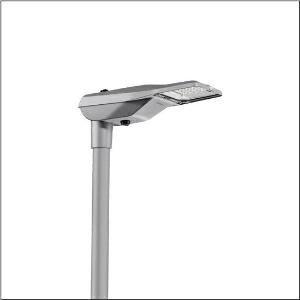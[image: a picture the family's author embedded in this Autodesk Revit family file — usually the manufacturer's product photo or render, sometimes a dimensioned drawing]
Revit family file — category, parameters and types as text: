
# Revit family: streetlight_sl_21_iq_micro___st1_0a_5xe1d51y08cb_5320
name_source: partatom
category: Lighting Fixtures
units: mm (PartAtom-declared; Revit-internal decimal feet)

## family parameters
Cut with Voids When Loaded = No
Host = Face
Light Source = No
Part Type = Normal
Room Calculation Point = No
Round Connector Dimension = Use Diameter
Shared = No

## types (1)
- --- (1 x LED, 2530 lm, 19.1 W, 3000K)
    Apparent Load = 19 VA
    CIE Flux Codes = 37 72 97 100 100
    Color Rendering = 80
    Color Temperature = 3000K
    Default Elevation = 1800 mm
    Description = Streetlight SL 21 iQ micro, mast luminaire, primary light control with lens, of PMMA, primary optical cover: cover, of toughened safety glass, transparent, light distribution: ST1.0a, light emission: direct distribution, primary light characteristic: asymmetric, installation type: post-top, side-entry, LED, High Power LED, rated luminous flux: 2.530lm, luminous efficacy: 133lm/W, light colour: 830, colour temperature: 3000K, control gear: iQ-Street Remote, D4i with power reduction, control: pre-setting: logarithmic dimming characteristic, Street-Remote, Auto-Match, Temp-Guard, Lumen-Switch, Night-Set, Smart-Wire, Light-Fading, Desk-Remote (wireless, voltage-free reading and setting of iQ features in the workshop via application-optimized NFC function/RFID function), optimised constant luminous flux control (CLO 2.0), mains connection: 220..240V, AC, 50/60Hz, start of lifetime: 19W, end of service life: 20W, reduction: 9W, luminaire housing, of diecast aluminium, powder-coated, Siteco® metallic grey (DB 702S), corrosivity category C5 high according to DIN EN ISO 12944, please order mast flange separately, inclination adjustable: 0°, 5°, 10°, 15°, sealing non-destructively replaceable, multi-level sealing system, length: 528mm, width: 235mm, height: 110mm, mast flange for spigot size: 42mm (side-entry): 5XC10008XM4, 60/48mm (side-entry/post-top): 5XC10108XM2, 76/60mm (side-entry/post-top): 5XC10108XM1, mounting height: 4..8m, Smart Interface below and above, protection rating (complete): IP66, insulation class (complete): insulation class II (safety insulation), certification: CE, ENEC, ENEC+, VDE, impact resistance: IK10, permissible operating ambient temperature for outdoor applications: -40..+50°C, standard-compliant lighting for roads and squares, packaging unit: 1 piece

Light Distribution: ST1.0a
    Height = 110 mm
    Lamp = 1 x LED
    Lamp Light Flux = 2530 lm
    Lamp Power = 19.1 W
    Lamp count = 1
    Length = 528 mm
    Luminous efficacy = 132 lm/W
    Manufacturer = Siteco
    ModVariant = No
    Model = 5XE1D51Y08CB
    Number of Poles = 1
    OnlyDefault = Yes
    Power Factor = 1
    Product Name = Streetlight SL 21 iQ micro | ST1.0a
    Product group = mast luminaire | pylon top
    ProductGroupID = 6100
    Protection Class = Protection class II
    Protection Degree = IP 66
    RLX_Detail_Level = 1
    RLX_Emergency_Light_Flux = 0 lm
    RLX_Emergency_Type = 0
    RLX_Emergency_Type_DB = No
    RlxData = <blob elided: 98473 chars, md5=553108e6>
    Socket = socket
    Standby Power = 0 W
    System Light Flux = 2530 lm
    System Power = 19 W
    Type Comments = factory setting: luminous flux: 100 % | dim-lin: 254 | 387 mA
    Type Image = l_1007239.jpg
    URL = http://relux.com
    VarID = @adj_119285
    Voltage = 0 V
    Weight = 0.00 kg
    Width = 235 mm

## geometry (parser evidence)
native form markers: Blend x4, Sweep x10
no freeform markers — native parametric forms only
